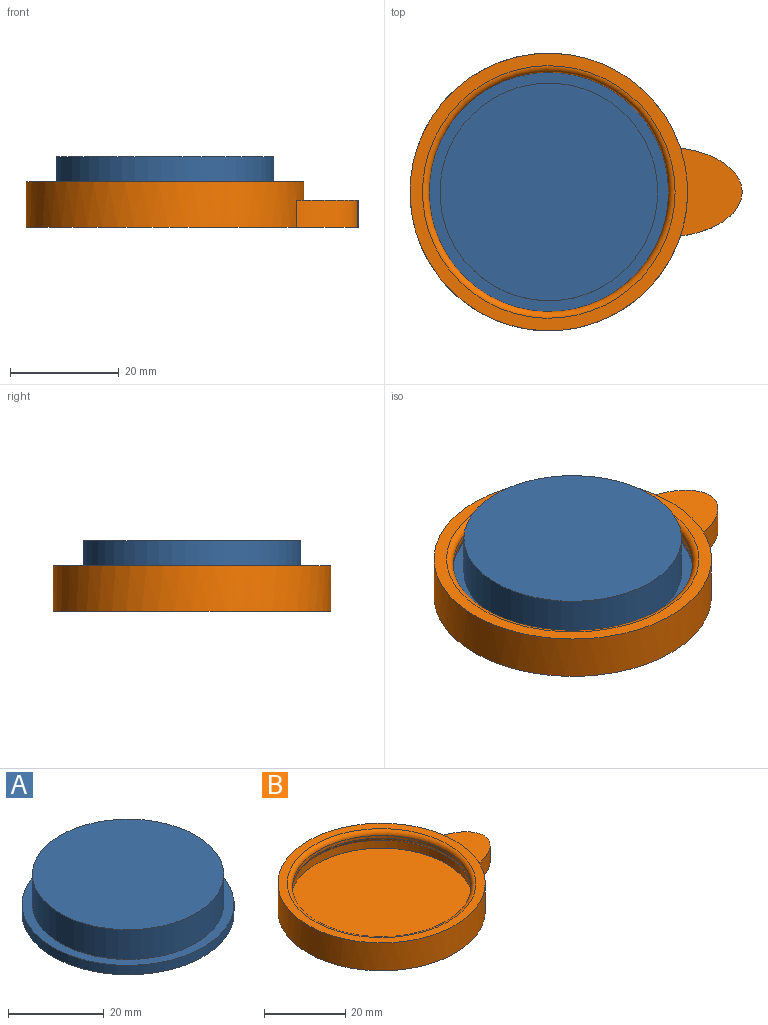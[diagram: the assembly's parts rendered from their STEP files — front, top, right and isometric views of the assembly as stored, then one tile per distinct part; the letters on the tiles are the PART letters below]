
ASSEMBLY  parts=2 mates=1
PART A: 5 faces, bbox 44.3x44.3x10 mm
  f0: cylinder r=20mm len=40mm, axis (0,0,-1), area 955mm2, adj f1,f3
  f1: plane 40x40mm, normal (0,0,1), area 1256.6mm2, adj f0
  f2: cylinder r=22.15mm len=44.3mm, axis (0,0,-1), area 334mm2, adj f3,f4
  f3: plane 44.3x44.3mm, normal (0,0,1), area 284.7mm2, adj f0,f2
  f4: plane 44.3x44.3mm, normal (0,0,-1), area 1541.3mm2, adj f2
PART B: 12 faces, bbox 61x51x8.4 mm
  f0: cylinder r=25.5mm len=51mm, axis (0,0,-1), area 1263.5mm2, adj f1,f2,f8,f10,f11
  f1: plane 61x51mm, normal (0,0,-1), area 2165.5mm2, adj f0,f8,f9,f10
  f2: plane 51x51mm, normal (0,0,1), area 351.9mm2, adj f0,f6
  f3: cylinder r=22mm len=44mm, axis (0,0,1), area 114.1mm2, adj f6,f7
  f4: plane 45x45mm, normal (0,0,1), area 1590.4mm2, adj f5
  f5: cylinder r=22.5mm len=45mm, axis (0,0,-1), area 339.3mm2, adj f4,f7
  f6: torus R=23.2mm, axis (0,0,1), area 265.7mm2, adj f2,f3
  f7: torus R=23.2mm, axis (0,0,-1), area 158.5mm2, adj f3,f5
  f8: extruded ~11.24x7.18mm, area 70.7mm2, adj f0,f1,f9,f11
  f9: cylinder r=5mm len=5mm, axis (0,0,-1), area 9.1mm2, adj f1,f8,f10,f11
  f10: extruded ~11.24x7.18mm, area 70.7mm2, adj f0,f1,f9,f11
  f11: plane 16.18x11.32mm, normal (0,0,1), area 122.6mm2, adj f0,f8,f9,f10
PLACE A t=(-0.62,0.15,-0.68)mm
PLACE B t=(-0.62,0.15,-3.68)mm
MATE fastened A.f0 <-> B.f0  axis (0,0,-1) through (-0.62,0.15,-0.68)mm
